# Revit family: Lighting_Fixture-Wall-Astro-7161_Karlaxxxxx
name_source: partatom
category: Lighting Fixtures
revit_build: Autodesk Revit LT 2014 (Build: 20130308_1515(x64)
units: mm (PartAtom-declared; Revit-internal decimal feet)

## types (1)
- 7161 Karla
    Apparent Load = 4 VA
    Assembly Code = D5020200
    Casing Material = Astro - Aluminium - Chrome Finish
    Class = 2
    Color Filter = 16777215
    Description = Wall Light
    Dimmable = No
    Dimming Lamp Color Temperature Shift = <None>
    Emit Shape Visible in Rendering = No
    Emit from Rectangle Length = 48 mm  [stored 0.15748 ft]
    Emit from Rectangle Width = 313.5 mm  [stored 1.02854 ft]
    Height = 329 mm  [stored 1.0794 ft]
    IP Rating = IP44
    Lamp = LED
    Lamp included = Yes
    Length = 90 mm  [stored 0.295276 ft]
    Light Source From Wall = 65 mm  [stored 0.213255 ft]
    Manufacturer = Astro Lighting Ltd, CM20 2DP
    Model = 7161 Karla
    Mountable on normally flammable surfaces = Yes
    Number of Poles = 1
    Photometric Web File = KARLA.ies
    Product Documentation = http://www.astrolighting.co.uk
    Suitable for bathroom zone = Zones 2 and 3
    Tilt Angle = 90.00°
    Type Comments = Includes integral LED driver
    URL = www.astrolighting.co.uk
    Voltage = 230 V
    Wattage Comments = 3.5w
    Weight = 0.97kg
    Width = 50 mm  [stored 0.164042 ft]

note: [stored X ft] marks values corroborated as IEEE doubles in the binary element streams (Revit-internal decimal feet)

## geometry (parser evidence)
native form markers: Sweep x1
no freeform markers — native parametric forms only
